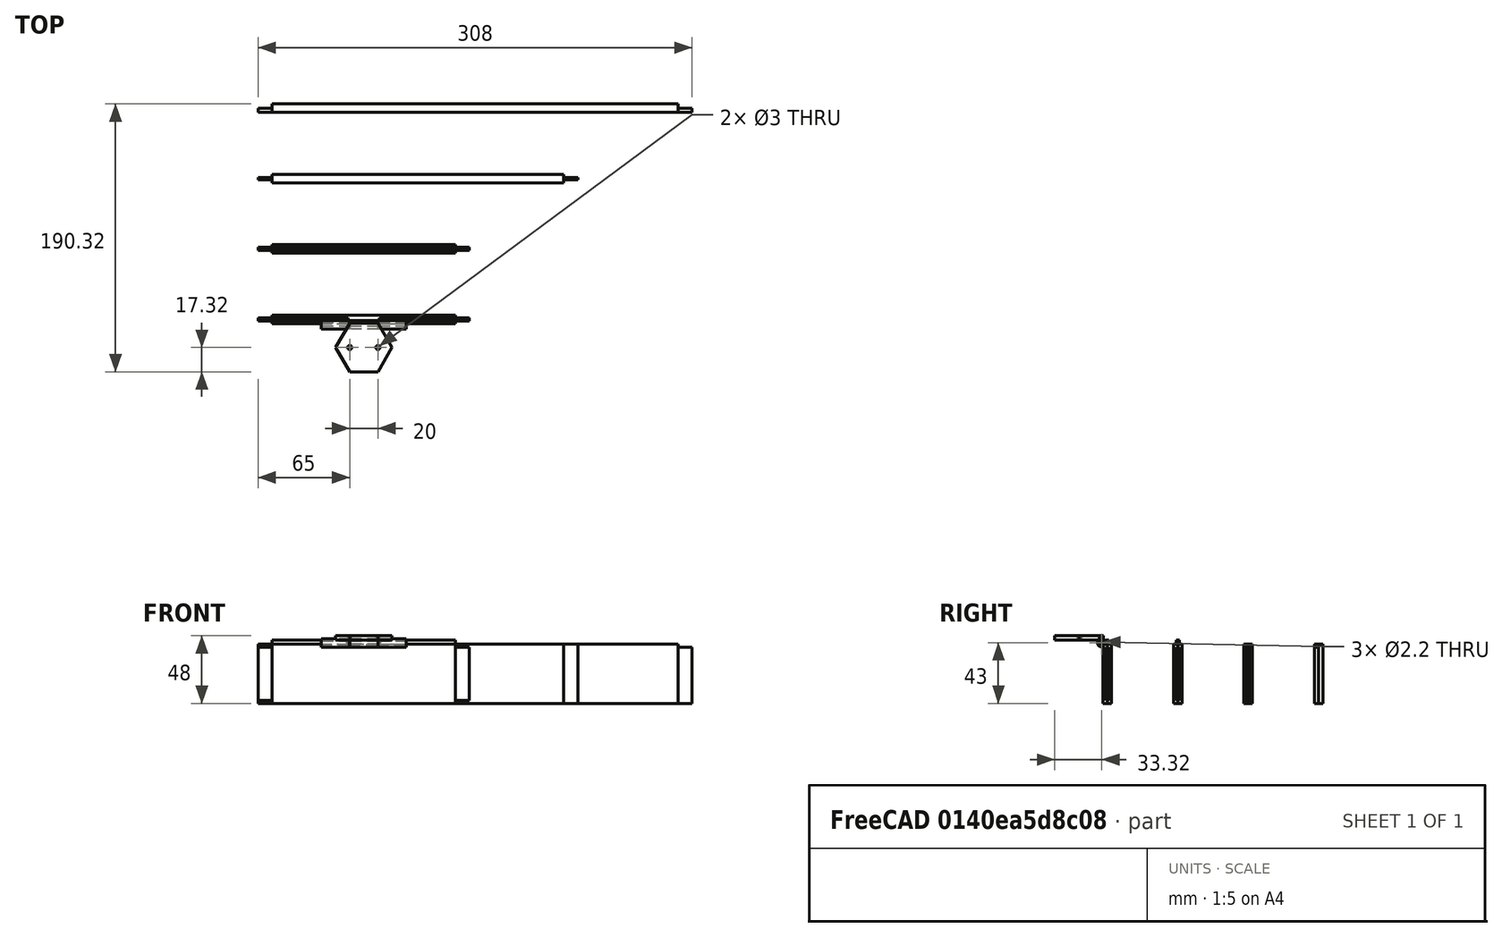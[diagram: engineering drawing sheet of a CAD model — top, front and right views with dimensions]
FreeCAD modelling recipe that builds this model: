
FCSTD DOCUMENT  (FreeCAD 0.21R33771 (Git))
Label: sides and shelves
License: All rights reserved
LicenseURL: http://en.wikipedia.org/wiki/All_rights_reserved
objects: Part::Box×17, Part::Cylinder×9, Part::Cut×8, Part::Compound×5, Part::Chamfer×2, Part::RegularPolygon×1, Part::Extrusion×1
note: 43 computed .brp shape members not serialized (recipe doc carries the construction recipe); baked Part::Feature solids carry a one-line shape summary decoded from their .brp

FEATURE [Part::Box] short_shelve_main
  AttacherType = Attacher::AttachEngine3D
  Height = 42
  Length = 207
  Width = 6
FEATURE [Part::Box] short_shelve_left
  AttacherType = Attacher::AttachEngine3D
  Height = 42
  Length = 10
  Placement = pos=(-10,2.2,0) rot=(1,0,0;0rad)
  Width = 1.6
FEATURE [Part::Box] short_shelve_right
  AttacherType = Attacher::AttachEngine3D
  Height = 42
  Length = 10
  Placement = pos=(207,2.2,0) rot=(1,0,0;0rad)
  Width = 1.6
FEATURE [Part::Compound] short_shelve_compound
  Links = -> [short_shelve_main,short_shelve_left,short_shelve_right]
  Placement = pos=(0,50,0) rot=(0,0,1;0rad)
FEATURE [Part::Box] long_shelve_main
  AttacherType = Attacher::AttachEngine3D
  Height = 42
  Length = 288
  Width = 6
FEATURE [Part::Box] long_shelve_left
  AttacherType = Attacher::AttachEngine3D
  Height = 40
  Length = 10
  Placement = pos=(-10,0,0) rot=(1,0,0;0rad)
  Width = 3
FEATURE [Part::Box] long_shelve_right
  AttacherType = Attacher::AttachEngine3D
  Height = 40
  Length = 10
  Placement = pos=(288,0,0) rot=(1,0,0;0rad)
  Width = 3
FEATURE [Part::Compound] long_shelve_compound
  Links = -> [long_shelve_main,long_shelve_left,long_shelve_right]
  Placement = pos=(0,100,0) rot=(0,0,1;0rad)
FEATURE [Part::Box] side_main
  AttacherType = Attacher::AttachEngine3D
  Height = 42
  Length = 130
  Width = 6
FEATURE [Part::Box] side_left
  AttacherType = Attacher::AttachEngine3D
  Height = 38
  Length = 10
  Placement = pos=(-10,1.95,2) rot=(1,0,0;0rad)
  Width = 2.1
FEATURE [Part::Box] side_right
  AttacherType = Attacher::AttachEngine3D
  Height = 38
  Length = 10
  Placement = pos=(130,1.95,2) rot=(1,0,0;0rad)
  Width = 2.1
FEATURE [Part::Box] side_ridge
  AttacherType = Attacher::AttachEngine3D
  Height = 3
  Length = 130
  Placement = pos=(0,2,42) rot=(1,0,0;0rad)
  Width = 2
FEATURE [Part::Compound] side_compound
  Links = -> [side_main,side_left,side_right,side_ridge]
FEATURE [Part::Box] side_hinge_main
  AttacherType = Attacher::AttachEngine3D
  Height = 42
  Length = 130
  Width = 6
FEATURE [Part::Box] side_hinge_left
  AttacherType = Attacher::AttachEngine3D
  Height = 38
  Length = 10
  Placement = pos=(-10,1.95,2) rot=(1,0,0;0rad)
  Width = 2.1
FEATURE [Part::Box] side_hinge_right
  AttacherType = Attacher::AttachEngine3D
  Height = 38
  Length = 10
  Placement = pos=(130,1.95,2) rot=(1,0,0;0rad)
  Width = 2.1
FEATURE [Part::Box] side_hinge_rid1
  AttacherType = Attacher::AttachEngine3D
  Height = 3
  Length = 54
  Placement = pos=(0,2,42) rot=(1,0,0;0rad)
  Width = 2
FEATURE [Part::Box] side_hinge_rid2
  AttacherType = Attacher::AttachEngine3D
  Height = 3
  Length = 54
  Placement = pos=(76,2,42) rot=(1,0,0;0rad)
  Width = 2
FEATURE [Part::Chamfer] Chamfer_ridg1
  Base = -> side_hinge_rid1
  Edges = 1 edges: [Edge6 r1=2.99 r2=2]
FEATURE [Part::Chamfer] Chamfer_ridg2
  Base = -> side_hinge_rid2
  Edges = 1 edges: [Edge2 r1=2.99 r2=2]
FEATURE [Part::Cylinder] hinge_cyllo
  Angle = 360
  AttacherType = Attacher::AttachEngine3D
  FirstAngle = 0
  Height = 20
  Placement = pos=(34.9,-1,43) rot=(0,1,0;1.5708rad)
  Radius = 3
  SecondAngle = 0
FEATURE [Part::Cylinder] hinge_cylli
  Angle = 360
  AttacherType = Attacher::AttachEngine3D
  FirstAngle = 0
  Height = 20
  Placement = pos=(34.9,-1,43) rot=(0,1,0;1.5708rad)
  Radius = 1.1
  SecondAngle = 0
FEATURE [Part::Cut] hinge_left
  Base = -> hinge_cyllo
  Tool = -> hinge_cylli
FEATURE [Part::Cylinder] hinge_cylro
  Angle = 360
  AttacherType = Attacher::AttachEngine3D
  FirstAngle = 0
  Height = 20
  Placement = pos=(75.1,-1,43) rot=(0,1,0;1.5708rad)
  Radius = 3
  SecondAngle = 0
FEATURE [Part::Cylinder] hinge_cylri
  Angle = 360
  AttacherType = Attacher::AttachEngine3D
  FirstAngle = 0
  Height = 20
  Placement = pos=(75.1,-1,43) rot=(0,1,0;1.5708rad)
  Radius = 1.1
  SecondAngle = 0
FEATURE [Part::Cut] hinge_right
  Base = -> hinge_cylro
  Tool = -> hinge_cylri
FEATURE [Part::Cylinder] hinge_cut
  Angle = 360
  AttacherType = Attacher::AttachEngine3D
  FirstAngle = 0
  Height = 20.2
  Placement = pos=(54.9,-1,43) rot=(0,1,0;1.5708rad)
  Radius = 3.1
  SecondAngle = 0
FEATURE [Part::Cut] side_main_cut
  Base = -> side_hinge_main
  Tool = -> hinge_cut
FEATURE [Part::Compound] side_hinge_compound
  Links = -> [side_main_cut,side_hinge_left,side_hinge_right,Chamfer_ridg1,Chamfer_ridg2,hinge_right,hinge_left]
  Placement = pos=(0,-50,0) rot=(0,0,1;0rad)
FEATURE [Part::Cylinder] hinge_cylmo
  Angle = 360
  AttacherType = Attacher::AttachEngine3D
  FirstAngle = 0
  Height = 20
  Placement = pos=(55,-1,43) rot=(0,1,0;1.5708rad)
  Radius = 3
  SecondAngle = 0
FEATURE [Part::Cylinder] hinge_cylmi
  Angle = 360
  AttacherType = Attacher::AttachEngine3D
  FirstAngle = 0
  Height = 20
  Placement = pos=(55,-1,43) rot=(0,1,0;1.5708rad)
  Radius = 1.1
  SecondAngle = 0
FEATURE [Part::Cut] hinge_middle
  Base = -> hinge_cylmo
  Tool = -> hinge_cylmi
FEATURE [Part::RegularPolygon] hexleaf
  AttacherType = Attacher::AttachEngine3D
  Circumradius = 20
  Placement = pos=(65,-17,45) rot=(0,0,1;0rad)
  Polygon = 6
FEATURE [Part::Extrusion] extleaf
  Base = -> hexleaf
  Dir = (0,0,1)
  DirMode = 0
  FaceMakerClass = Part::FaceMakerBullseye
  LengthFwd = 3
  LengthRev = 0
  Solid = true
  Symmetric = false
FEATURE [Part::Box] side_hinge_left001
  AttacherType = Attacher::AttachEngine3D
  Height = 1
  Length = 7
  Placement = pos=(48,-3.5,45) rot=(1,0,0;0rad)
  Width = 4
FEATURE [Part::Box] side_hinge_right001
  AttacherType = Attacher::AttachEngine3D
  Height = 1
  Length = 7
  Placement = pos=(75,-3.5,45) rot=(1,0,0;0rad)
  Width = 4
FEATURE [Part::Cut] cutover1
  Base = -> extleaf
  Tool = -> side_hinge_left001
FEATURE [Part::Cut] cutover2
  Base = -> cutover1
  Tool = -> side_hinge_right001
FEATURE [Part::Cylinder] hole1
  Angle = 360
  AttacherType = Attacher::AttachEngine3D
  FirstAngle = 0
  Height = 10
  Placement = pos=(55,-17,42) rot=(1,0,0;0rad)
  Radius = 1.5
  SecondAngle = 0
FEATURE [Part::Cylinder] hole2
  Angle = 360
  AttacherType = Attacher::AttachEngine3D
  FirstAngle = 0
  Height = 10
  Placement = pos=(75,-17,42) rot=(1,0,0;0rad)
  Radius = 1.5
  SecondAngle = 0
FEATURE [Part::Cut] cuthole1
  Base = -> cutover2
  Tool = -> hole1
FEATURE [Part::Cut] cuthole2
  Base = -> cuthole1
  Tool = -> hole2
FEATURE [Part::Compound] leaf_compound
  Links = -> [cuthole2,hinge_middle]
  Placement = pos=(0,-50,0) rot=(0,0,1;0rad)
